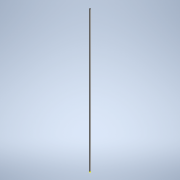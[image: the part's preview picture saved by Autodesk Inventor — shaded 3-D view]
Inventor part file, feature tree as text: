
AUTODESK INVENTOR PART (.ipt)
format: ipt  version: 2021 (Build 250183000, 183)  size: 94,208 bytes
history: native  units: mm
features: sketch x2, extrude x1
ambient origin geometry x8: Origin, YZ Plane, XZ Plane, XY Plane, X Axis, Y Axis, Z Axis, Center Point
bodies: Solid1 (feature_tree)
feature tree (3):
  extrude  "Extrusion1"  Depth=13.0mm
  sketch  "Sketch2"  dims[d2=2000.0mm d3=0.0mm]
  sketch  "Sketch1"  dims[d0=13.0mm d1=13.0mm]
